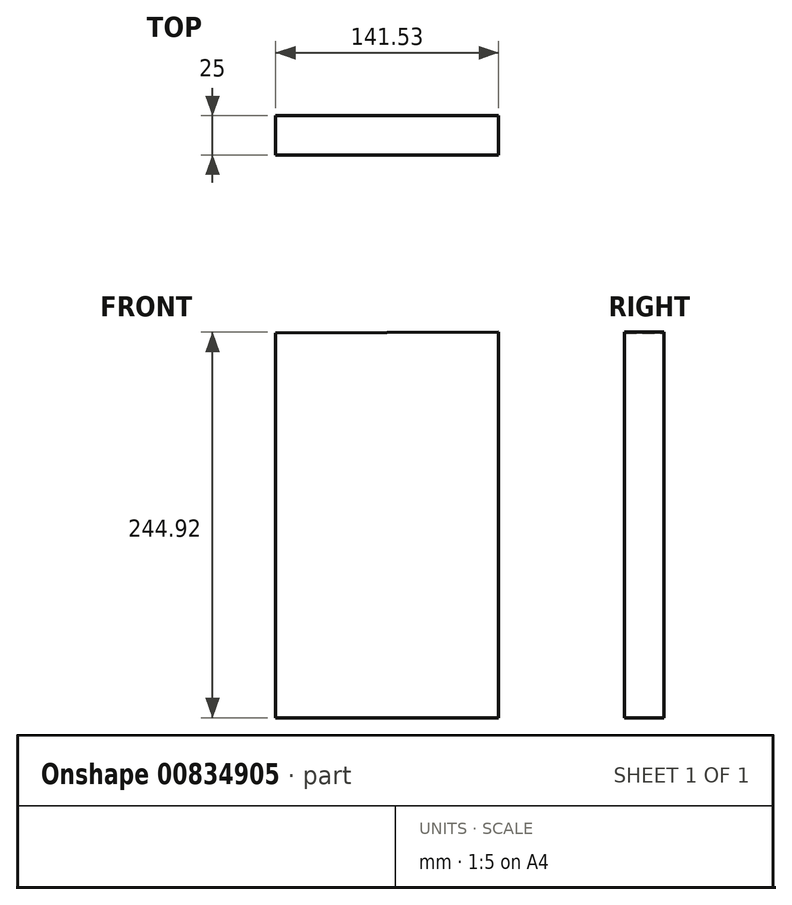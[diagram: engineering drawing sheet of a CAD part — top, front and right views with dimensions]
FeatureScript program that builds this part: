
annotation { "Feature Type Name" : "Feature", "Feature Type Description" : "" }
export const myFeature = defineFeature(function(context is Context, id is Id, definition is map)
    precondition{}
    {
        {
            var Q0;
            Q0=qCreatedBy(makeId("Front.planeOp"),FACE);
            var sketch = newSketch(context, id + "F0", { "sketchPlane" : qUnion([Q0])});
            skLineSegment(sketch, "E0", {"start": v(-75.2, 76.68) * mm, "end": v(-75.2, -167.67) * mm});
            skLineSegment(sketch, "E1", {"start": v(-75.2, -167.67) * mm, "end": v(66.33, -167.67) * mm});
            skLineSegment(sketch, "E2", {"start": v(66.33, -167.67) * mm, "end": v(66.33, 77.25) * mm});
            skLineSegment(sketch, "E3", {"start": v(66.33, 77.25) * mm, "end": v(-75.2, 76.68) * mm});
            skSolve(sketch);
        }
        {
            var Q0;
            Q0 = qSketchRegion(id + "F0", true);
            extrude(context, id + "F1", {"entities" : qUnion([Q0]), "depth" : 25 * mm, "offsetDistance" : 25 * mm});
        }
    });
